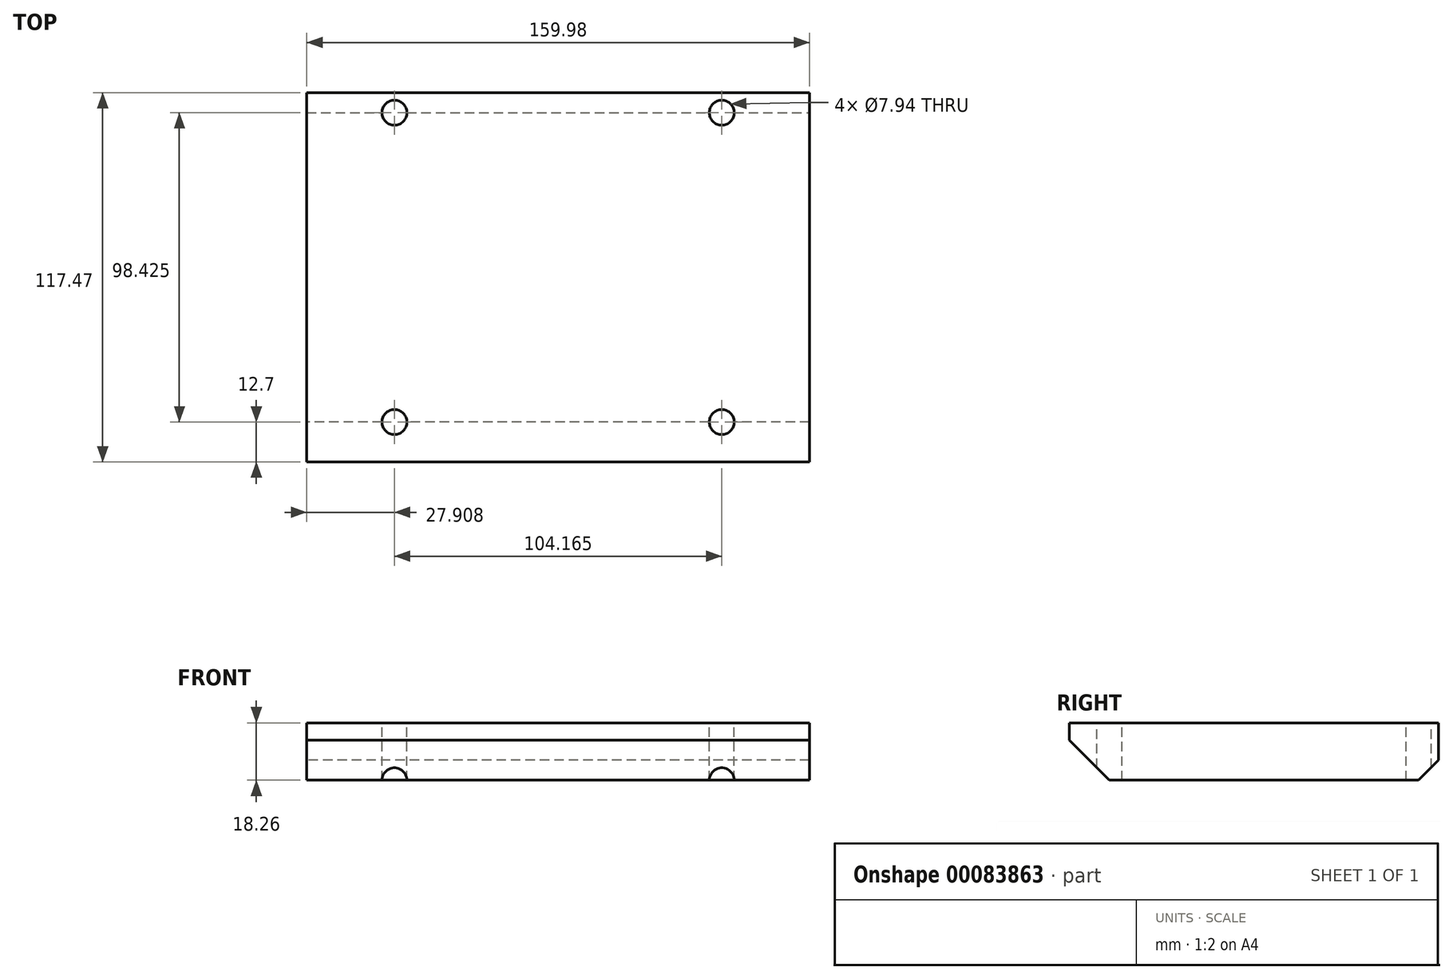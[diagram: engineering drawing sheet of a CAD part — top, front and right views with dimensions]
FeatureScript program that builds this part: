
annotation { "Feature Type Name" : "Feature", "Feature Type Description" : "" }
export const myFeature = defineFeature(function(context is Context, id is Id, definition is map)
    precondition{}
    {
        {
            var Q0;
            Q0=qCreatedBy(makeId("Top.planeOp"),FACE);
            var sketch = newSketch(context, id + "F0", { "sketchPlane" : qUnion([Q0])});
            skLineSegment(sketch, "E0.bottom", {"start": v(0, 0) * mm, "end": v(159.98, 0) * mm});
            skLineSegment(sketch, "E0.top", {"start": v(0, 117.47) * mm, "end": v(159.98, 117.47) * mm});
            skLineSegment(sketch, "E0.left", {"start": v(0, 0) * mm, "end": v(0, 117.47) * mm});
            skLineSegment(sketch, "E0.right", {"start": v(159.98, 0) * mm, "end": v(159.98, 117.48) * mm});
            skSolve(sketch);
        }
        {
            var Q0;
            Q0=makeQuery(id+"F0.imprint","IMPRINT",FACE,{"disambiguationData":[TD([[makeQuery(id+"F0.imprint","IMPRINT",EDGE,{"derivedFrom":sQuery(id+"F0.wireOp",EDGE,"E0.bottom")}),1.0]])]});
            extrude(context, id + "F1", {"entities" : qUnion([Q0]), "depth" : 18.26 * mm});
        }
        {
            var Q0;
            Q0=makeQuery(id+"F1.opExtrude","CAP_FACE",FACE,{"disambiguationData":[OSD([sQuery(id+"F0.wireOp",EDGE,"E0.bottom"),sQuery(id+"F0.wireOp",EDGE,"E0.top"),sQuery(id+"F0.wireOp",EDGE,"E0.left"),sQuery(id+"F0.wireOp",EDGE,"E0.right")])],"isStart":false});
            var sketch = newSketch(context, id + "F2", { "sketchPlane" : qUnion([Q0])});
            skCircle(sketch, "E1", {"center": v(27.9, 12.7) * mm, "radius": 3.97 * mm});
            skCircle(sketch, "E2", {"center": v(132.07, 12.7) * mm, "radius": 3.97 * mm});
            skSolve(sketch);
        }
        {
            var Q0;
            Q0=sQuery(id+"F2.wireOp",VERTEX,"E1.center");
            var Q1;
            Q1=sQuery(id+"F2.wireOp",VERTEX,"E2.center");
            var Q2;
            Q2=makeQuery(id+"F1.opExtrude","SWEPT_BODY",BODY,{"disambiguationData":[OSD([sQuery(id+"F0.wireOp",EDGE,"E0.bottom"),sQuery(id+"F0.wireOp",EDGE,"E0.top"),sQuery(id+"F0.wireOp",EDGE,"E0.left"),sQuery(id+"F0.wireOp",EDGE,"E0.right")])]});
            hole(context, id + "F3", {"style" : HoleStyle.SIMPLE, "endStyle" : HoleEndStyle.THROUGH, "holeDiameter" : 7.94 * mm, "locations" : qUnion([Q0, Q1]), "scope" : qUnion([Q2]), "isTappedThrough" : true});
        }
        {
            var Q0;
            Q0=makeQuery(id+"F1.opExtrude","CAP_FACE",FACE,{"disambiguationData":[OSD([sQuery(id+"F0.wireOp",EDGE,"E0.bottom"),sQuery(id+"F0.wireOp",EDGE,"E0.top"),sQuery(id+"F0.wireOp",EDGE,"E0.left"),sQuery(id+"F0.wireOp",EDGE,"E0.right")])],"isStart":false});
            var sketch = newSketch(context, id + "F4", { "sketchPlane" : qUnion([Q0])});
            skLineSegment(sketch, "E3", {"start": v(0, 117.47) * mm, "end": v(0, 111.12) * mm});
            skLineSegment(sketch, "E4", {"start": v(0, 111.12) * mm, "end": v(159.98, 111.12) * mm});
            skLineSegment(sketch, "E5", {"start": v(0, 111.12) * mm, "end": v(27.9, 111.12) * mm});
            skLineSegment(sketch, "E6", {"start": v(159.98, 111.12) * mm, "end": v(132.07, 111.12) * mm});
            skSolve(sketch);
        }
        {
            var Q0;
            Q0=sQuery(id+"F4.wireOp",VERTEX,"E5.end");
            var Q1;
            Q1=sQuery(id+"F4.wireOp",VERTEX,"E6.end");
            var Q2;
            Q2=makeQuery(id+"F1.opExtrude","SWEPT_BODY",BODY,{"disambiguationData":[OSD([sQuery(id+"F0.wireOp",EDGE,"E0.bottom"),sQuery(id+"F0.wireOp",EDGE,"E0.top"),sQuery(id+"F0.wireOp",EDGE,"E0.left"),sQuery(id+"F0.wireOp",EDGE,"E0.right")])]});
            hole(context, id + "F5", {"style" : HoleStyle.SIMPLE, "endStyle" : HoleEndStyle.THROUGH, "holeDiameter" : 7.94 * mm, "locations" : qUnion([Q0, Q1]), "scope" : qUnion([Q2]), "isTappedThrough" : true});
        }
        {
            var Q0;
            Q0=makeQuery(id+"F1.opExtrude","CAP_EDGE",EDGE,{"disambiguationData":[OSD([sQuery(id+"F0.wireOp",EDGE,"E0.bottom")])],"isStart":true});
            chamfer(context, id + "F6", {"entities" : qUnion([Q0]), "width" : 12.7 * mm, "tangentPropagation" : true});
        }
        {
            var Q0;
            Q0=makeQuery(id+"F1.opExtrude","CAP_EDGE",EDGE,{"disambiguationData":[OSD([sQuery(id+"F0.wireOp",EDGE,"E0.top")])],"isStart":true});
            chamfer(context, id + "F7", {"entities" : qUnion([Q0]), "width" : 6.35 * mm, "tangentPropagation" : true});
        }
    });
